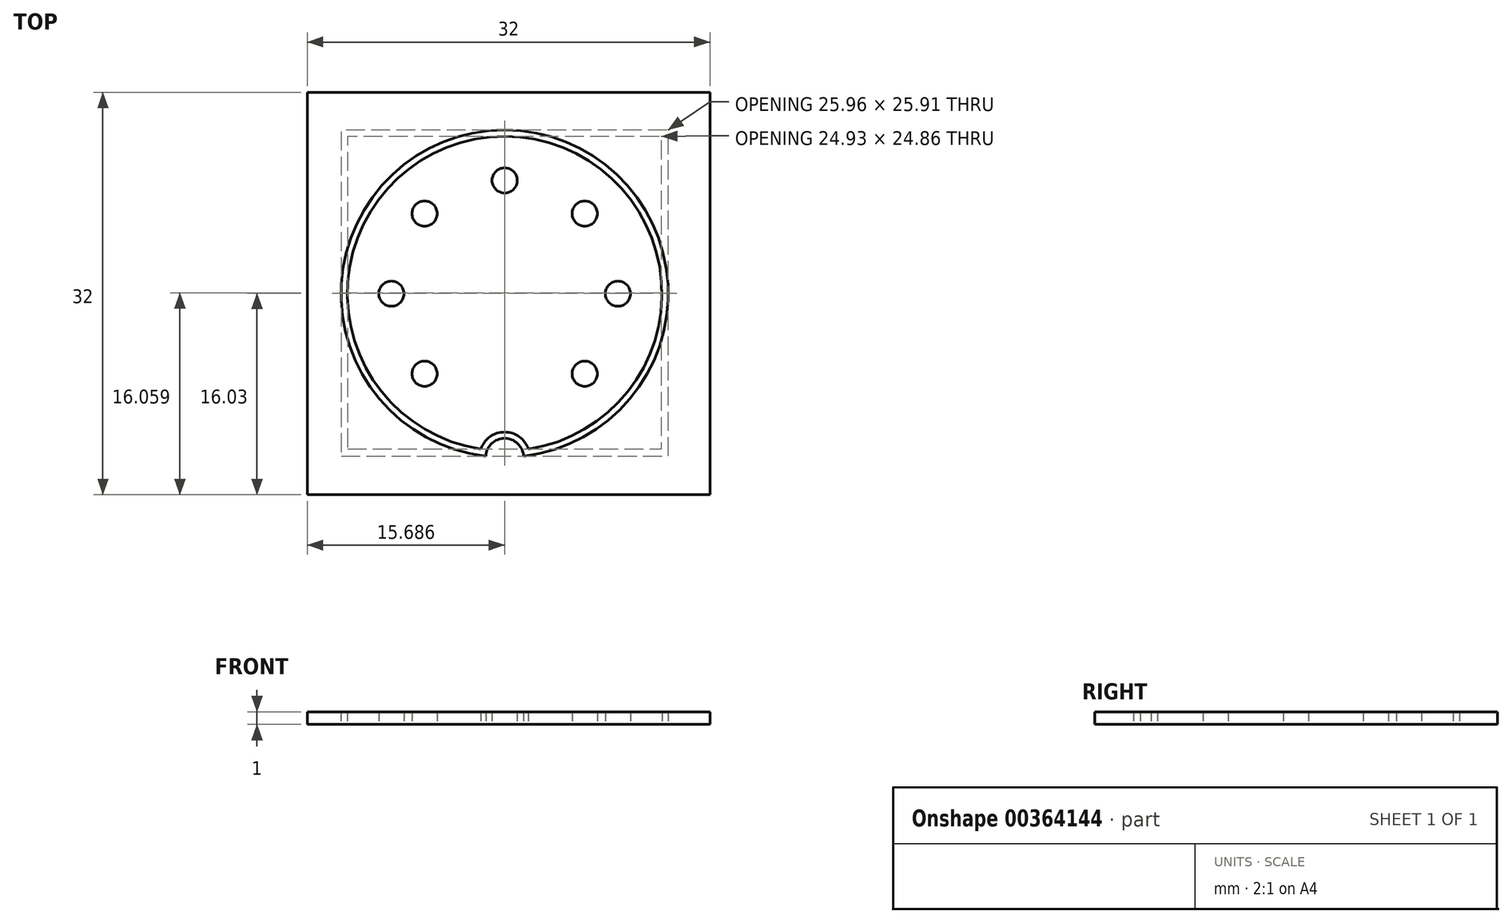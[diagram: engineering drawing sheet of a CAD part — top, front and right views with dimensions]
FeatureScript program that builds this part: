
annotation { "Feature Type Name" : "Feature", "Feature Type Description" : "" }
export const myFeature = defineFeature(function(context is Context, id is Id, definition is map)
    precondition{}
    {
        {
            var Q0;
            Q0=qCreatedBy(makeId("Top.planeOp"),FACE);
            var sketch = newSketch(context, id + "F0", { "sketchPlane" : qUnion([Q0])});
            skArc(sketch, "E0", {"start": v(1.88, -12.37) * mm, "mid": v(-0.01, 12.49) * mm, "end": v(-1.9, -12.37) * mm});
            skCircle(sketch, "E1", {"center": v(-0.01, 8.99) * mm, "radius": 1 * mm});
            skCircle(sketch, "E2", {"center": v(-9.01, -0.01) * mm, "radius": 1 * mm});
            skCircle(sketch, "E3", {"center": v(8.99, -0.01) * mm, "radius": 1 * mm});
            skCircle(sketch, "E4", {"center": v(-6.38, 6.35) * mm, "radius": 1 * mm});
            skCircle(sketch, "E5", {"center": v(6.35, 6.35) * mm, "radius": 1 * mm});
            skArc(sketch, "E6", {"start": v(1.48, -12.93) * mm, "mid": v(-0.01, 12.99) * mm, "end": v(-1.51, -12.93) * mm});
            skArc(sketch, "E7", {"start": v(1.48, -12.93) * mm, "mid": v(-0.01, -11.51) * mm, "end": v(-1.51, -12.93) * mm});
            skArc(sketch, "E8", {"start": v(1.88, -12.37) * mm, "mid": v(-0.01, -11.01) * mm, "end": v(-1.9, -12.37) * mm});
            skCircle(sketch, "E9", {"center": v(-6.38, -6.38) * mm, "radius": 1 * mm});
            skCircle(sketch, "E10", {"center": v(6.35, -6.38) * mm, "radius": 1 * mm});
            skLineSegment(sketch, "E11.bottom", {"start": v(16.3, -16) * mm, "end": v(-15.7, -16) * mm});
            skLineSegment(sketch, "E11.top", {"start": v(16.3, 16) * mm, "end": v(-15.7, 16) * mm});
            skLineSegment(sketch, "E11.left", {"start": v(16.3, -16) * mm, "end": v(16.3, 16) * mm});
            skLineSegment(sketch, "E11.right", {"start": v(-15.7, -16) * mm, "end": v(-15.7, 16) * mm});
            skPoint(sketch, "E11.middle", {"position": v(0.3, 0) * mm});
            skSolve(sketch);
        }
        {
            var Q0;
            Q0=makeQuery(id+"F0.imprint","IMPRINT",FACE,{"disambiguationData":[TD([[makeQuery(id+"F0.imprint","IMPRINT",EDGE,{"derivedFrom":sQuery(id+"F0.wireOp",EDGE,"E2")}),1.0]])]});
            var Q1;
            Q1=makeQuery(id+"F0.imprint","IMPRINT",FACE,{"disambiguationData":[TD([[makeQuery(id+"F0.imprint","IMPRINT",EDGE,{"derivedFrom":sQuery(id+"F0.wireOp",EDGE,"E4")}),1.0]])]});
            var Q2;
            Q2=makeQuery(id+"F0.imprint","IMPRINT",FACE,{"disambiguationData":[TD([[makeQuery(id+"F0.imprint","IMPRINT",EDGE,{"derivedFrom":sQuery(id+"F0.wireOp",EDGE,"E1")}),1.0]])]});
            var Q3;
            Q3=makeQuery(id+"F0.imprint","IMPRINT",FACE,{"disambiguationData":[TD([[makeQuery(id+"F0.imprint","IMPRINT",EDGE,{"derivedFrom":sQuery(id+"F0.wireOp",EDGE,"E5")}),1.0]])]});
            var Q4;
            Q4=makeQuery(id+"F0.imprint","IMPRINT",FACE,{"disambiguationData":[TD([[makeQuery(id+"F0.imprint","IMPRINT",EDGE,{"derivedFrom":sQuery(id+"F0.wireOp",EDGE,"E3")}),1.0]])]});
            var Q5;
            Q5=makeQuery(id+"F0.imprint","IMPRINT",FACE,{"disambiguationData":[TD([[makeQuery(id+"F0.imprint","IMPRINT",EDGE,{"derivedFrom":sQuery(id+"F0.wireOp",EDGE,"E10")}),1.0]])]});
            var Q6;
            Q6=makeQuery(id+"F0.imprint","IMPRINT",FACE,{"disambiguationData":[TD([[makeQuery(id+"F0.imprint","IMPRINT",EDGE,{"derivedFrom":sQuery(id+"F0.wireOp",EDGE,"E9")}),1.0]])]});
            var Q7;
            Q7=makeQuery(id+"F0.imprint","IMPRINT",FACE,{"disambiguationData":[TD([[makeQuery(id+"F0.imprint","IMPRINT",EDGE,{"derivedFrom":sQuery(id+"F0.wireOp",EDGE,"E0")}),-1.0]])]});
            extrude(context, id + "F1", {"entities" : qUnion([Q0, Q1, Q2, Q3, Q4, Q5, Q6, Q7]), "depth" : 1 * mm});
        }
        {
            var Q0;
            Q0 = qSketchRegion(id + "F0", true);
            extrude(context, id + "F2", {"entities" : qUnion([Q0]), "depth" : 1 * mm});
        }
    });
